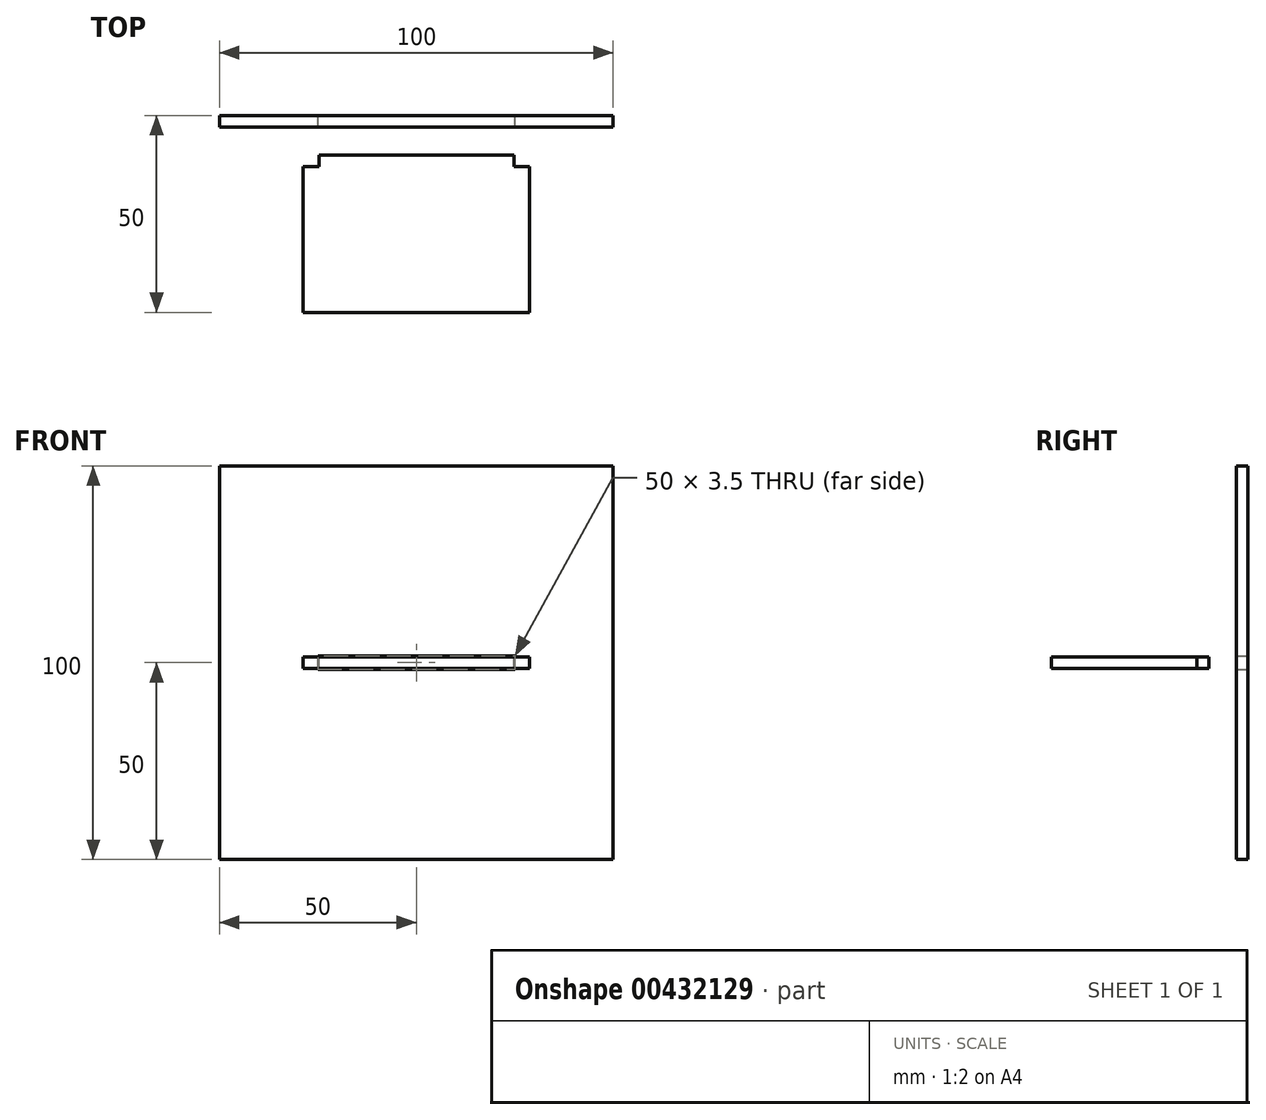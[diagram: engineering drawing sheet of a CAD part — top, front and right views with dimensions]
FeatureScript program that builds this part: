
annotation { "Feature Type Name" : "Feature", "Feature Type Description" : "" }
export const myFeature = defineFeature(function(context is Context, id is Id, definition is map)
    precondition{}
    {
        {
            var Q0;
            Q0=qCreatedBy(makeId("Front.planeOp"),FACE);
            var sketch = newSketch(context, id + "F0", { "sketchPlane" : qUnion([Q0])});
            skLineSegment(sketch, "E0.bottom", {"start": v(50, -50) * mm, "end": v(-50, -50) * mm});
            skLineSegment(sketch, "E0.top", {"start": v(50, 50) * mm, "end": v(-50, 50) * mm});
            skLineSegment(sketch, "E0.left", {"start": v(50, -50) * mm, "end": v(50, 50) * mm});
            skLineSegment(sketch, "E0.right", {"start": v(-50, -50) * mm, "end": v(-50, 50) * mm});
            skPoint(sketch, "E0.middle", {"position": v(0, 0) * mm});
            skLineSegment(sketch, "E1.bottom", {"start": v(25, -1.75) * mm, "end": v(-25, -1.75) * mm});
            skLineSegment(sketch, "E1.top", {"start": v(25, 1.75) * mm, "end": v(-25, 1.75) * mm});
            skLineSegment(sketch, "E1.left", {"start": v(25, -1.75) * mm, "end": v(25, 1.75) * mm});
            skLineSegment(sketch, "E1.right", {"start": v(-25, -1.75) * mm, "end": v(-25, 1.75) * mm});
            skSolve(sketch);
        }
        {
            var Q0;
            Q0=makeQuery(id+"F0.imprint","IMPRINT",FACE,{"disambiguationData":[TD([[makeQuery(id+"F0.imprint","IMPRINT",EDGE,{"derivedFrom":sQuery(id+"F0.wireOp",EDGE,"E0.bottom")}),-1.0]])]});
            extrude(context, id + "F1", {"entities" : qUnion([Q0]), "depth" : 3 * mm});
        }
        {
            var Q0;
            Q0=qCreatedBy(makeId("Front.planeOp"),FACE);
            cPlane(context, id + "F2", {"entities" : qUnion([Q0]), "cplaneType" : CPlaneType.OFFSET, "offset" : 10 * mm, "width" : 152.4 * mm, "height" : 152.4 * mm});
        }
        {
            var Q0;
            Q0=qCreatedBy(id+"F2.planeOp",FACE);
            var sketch = newSketch(context, id + "F3", { "sketchPlane" : qUnion([Q0])});
            skLineSegment(sketch, "E2.0", {"start": v(24.75, 1.5) * mm, "end": v(-24.75, 1.5) * mm});
            skLineSegment(sketch, "E2.1", {"start": v(24.75, -1.5) * mm, "end": v(24.75, 1.5) * mm});
            skLineSegment(sketch, "E2.2", {"start": v(24.75, -1.5) * mm, "end": v(-24.75, -1.5) * mm});
            skLineSegment(sketch, "E2.3", {"start": v(-24.75, -1.5) * mm, "end": v(-24.75, 1.5) * mm});
            skSolve(sketch);
        }
        {
            var Q0;
            Q0=makeQuery(id+"F3.imprint","IMPRINT",FACE,{"disambiguationData":[TD([[makeQuery(id+"F3.imprint","IMPRINT",EDGE,{"derivedFrom":sQuery(id+"F3.wireOp",EDGE,"E2.0")}),1.0]])]});
            extrude(context, id + "F4", {"entities" : qUnion([Q0]), "depth" : 40 * mm});
        }
        {
            var Q0;
            Q0=makeQuery(id+"F4.opExtrude","CAP_FACE",FACE,{"disambiguationData":[OSD([sQuery(id+"F3.wireOp",EDGE,"E2.0"),sQuery(id+"F3.wireOp",EDGE,"E2.1"),sQuery(id+"F3.wireOp",EDGE,"E2.2"),sQuery(id+"F3.wireOp",EDGE,"E2.3")])],"isStart":false});
            var sketch = newSketch(context, id + "F5", { "sketchPlane" : qUnion([Q0])});
            skLineSegment(sketch, "E3.bottom", {"start": v(-24.75, 1.5) * mm, "end": v(-28.75, 1.5) * mm});
            skLineSegment(sketch, "E3.top", {"start": v(-24.75, -1.5) * mm, "end": v(-28.75, -1.5) * mm});
            skLineSegment(sketch, "E3.left", {"start": v(-24.75, 1.5) * mm, "end": v(-24.75, -1.5) * mm});
            skLineSegment(sketch, "E3.right", {"start": v(-28.75, 1.5) * mm, "end": v(-28.75, -1.5) * mm});
            skLineSegment(sketch, "E4.bottom", {"start": v(24.75, 1.5) * mm, "end": v(28.75, 1.5) * mm});
            skLineSegment(sketch, "E4.top", {"start": v(24.75, -1.5) * mm, "end": v(28.75, -1.5) * mm});
            skLineSegment(sketch, "E4.left", {"start": v(24.75, 1.5) * mm, "end": v(24.75, -1.5) * mm});
            skLineSegment(sketch, "E4.right", {"start": v(28.75, 1.5) * mm, "end": v(28.75, -1.5) * mm});
            skSolve(sketch);
        }
        {
            var Q0;
            Q0 = qSketchRegion(id + "F5", true);
            extrude(context, id + "F6", {"entities" : qUnion([Q0]), "operationType" : NewBodyOperationType.ADD, "oppositeDirection" : true, "depth" : 37 * mm});
        }
    });
